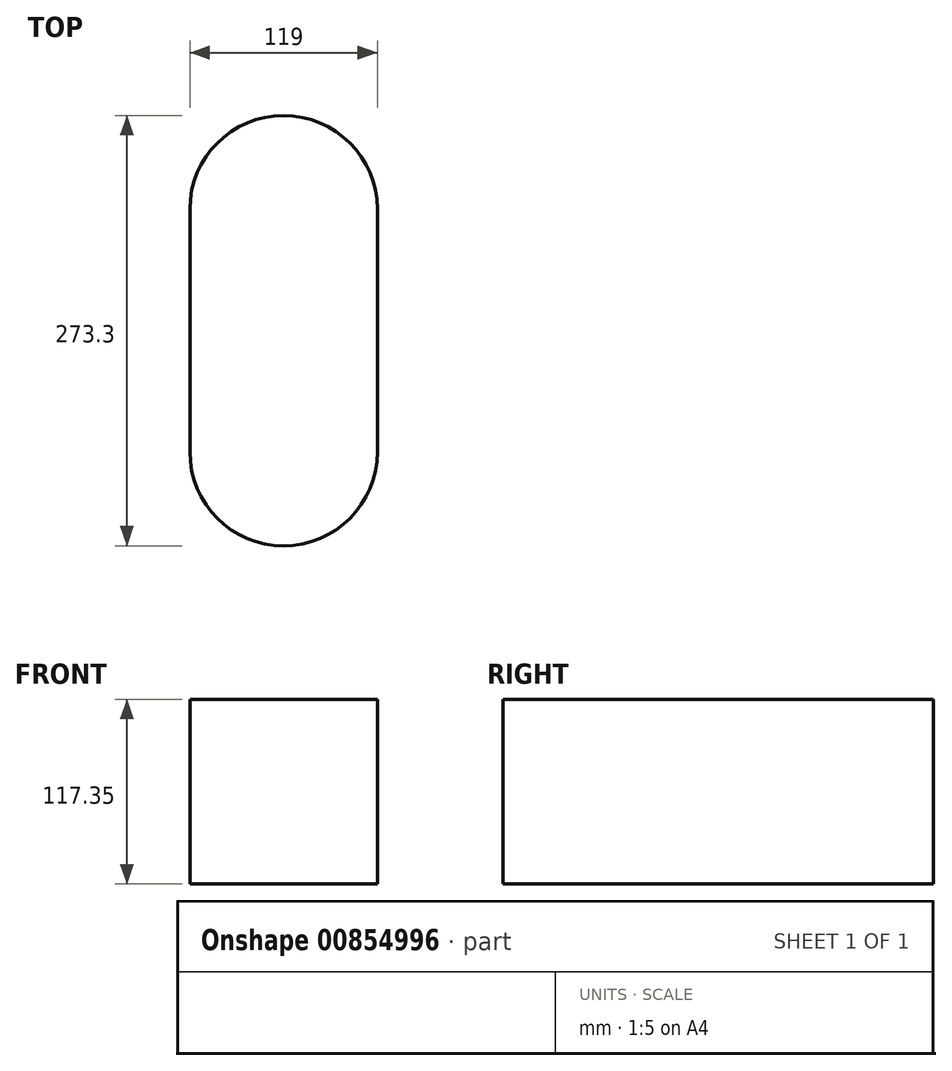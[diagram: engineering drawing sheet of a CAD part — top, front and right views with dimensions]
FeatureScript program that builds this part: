
annotation { "Feature Type Name" : "Feature", "Feature Type Description" : "" }
export const myFeature = defineFeature(function(context is Context, id is Id, definition is map)
    precondition{}
    {
        {
            var Q0;
            Q0=qCreatedBy(makeId("Top.planeOp"),FACE);
            var sketch = newSketch(context, id + "F0", { "sketchPlane" : qUnion([Q0])});
            skArc(sketch, "E0", {"start": v(59.5, 0) * mm, "mid": v(0, 59.5) * mm, "end": v(-59.5, 0) * mm});
            skLineSegment(sketch, "E1", {"start": v(-103.18, -77.15) * mm, "end": v(125.6, -77.15) * mm, "construction": true});
            skArc(sketch, "E2.MirrorC", {"start": v(59.5, -154.3) * mm, "mid": v(0, -213.8) * mm, "end": v(-59.5, -154.3) * mm});
            skLineSegment(sketch, "E3", {"start": v(59.5, -154.3) * mm, "end": v(59.5, 0) * mm});
            skLineSegment(sketch, "E4", {"start": v(-59.5, -154.3) * mm, "end": v(-59.5, 0) * mm});
            skSolve(sketch);
        }
        {
            var Q0;
            Q0 = qSketchRegion(id + "F0", true);
            extrude(context, id + "F1", {"entities" : qUnion([Q0]), "depth" : 117.35 * mm, "offsetDistance" : 25.4 * mm});
        }
    });
